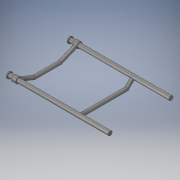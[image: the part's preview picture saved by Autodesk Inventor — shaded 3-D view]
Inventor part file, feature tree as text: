
AUTODESK INVENTOR PART (.ipt)
format: ipt  version: 2018 (Build 220112000, 112)  size: 161,280 bytes
history: native  units: in
note: dims shown in document units (in); Inventor stores cm internally (conversion verified against a paired STEP export)
features: sketch x7, extrude x3, sweep x2, plane x1
ambient origin geometry x8: Origin, YZ Plane, XZ Plane, XY Plane, X Axis, Y Axis, Z Axis, Center Point
bodies: Solid1 (feature_tree)
feature tree (13):
  sweep  "Sweep1"
  plane  "Work Plane1"
  sweep  "Sweep2"
  extrude  "Extrusion1"  TaperAngle=0.0deg  [1 undecoded]
  extrude  "Extrusion2"  Depth=15.0in
  extrude  "Extrusion3"  Depth=12.5in
  sketch  "Sketch1"  dims[d0=1.0in d1=3.5in]
  sketch  "Sketch2"  dims[d2=7.0in d3=16.25in]
  sketch  "Sketch3"  dims[d5=5.0in d6=0.0in d7=0.0in]
  sketch  "Sketch4"  dims[d8=15.0in d9=15.0in]
  sketch  "Sketch5"  dims[d10=1.0in d11=12.5in]
  sketch  "Sketch6"  dims[d13=0.0in]
  sketch  "Sketch7"  dims[d14=0.0in d15=0.0in d16=1.13in d17=25.0in d18=2.0in d19=0.0in d20=0.0in d21=1.56in d22=1.125in d23=0.0in d24=0.25in d25=0.0in d26=0.7719in]
note: 1 required parameter value undecoded (feature->parameter linkage not recoverable at this tier; creation-order binding heuristic only, values carry confidence <= 0.55)
